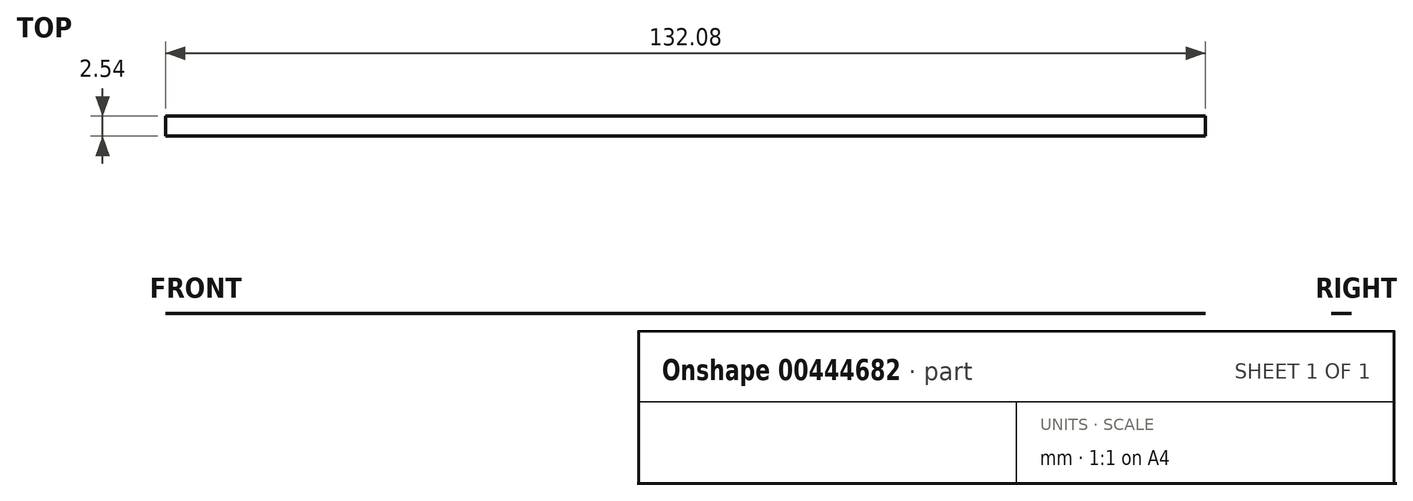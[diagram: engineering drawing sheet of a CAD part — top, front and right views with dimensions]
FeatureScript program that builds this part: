
annotation { "Feature Type Name" : "Feature", "Feature Type Description" : "" }
export const myFeature = defineFeature(function(context is Context, id is Id, definition is map)
    precondition{}
    {
        {
            var Q0;
            Q0=qCreatedBy(makeId("Front.planeOp"),FACE);
            var sketch = newSketch(context, id + "F0", { "sketchPlane" : qUnion([Q0])});
            skLineSegment(sketch, "E0", {"start": v(-67.35, 0) * mm, "end": v(64.73, 0) * mm});
            skSolve(sketch);
        }
        {
            var Q0;
            Q0 = qSketchRegion(id + "F0", true);
            var Q1;
            Q1=sQuery(id+"F0.wireOp",EDGE,"E0");
            extrude(context, id + "F1", {"entities" : qUnion([Q0]), "bodyType" : ToolBodyType.SURFACE, "surfaceEntities" : qUnion([Q1]), "depth" : 2.54 * mm});
        }
    });
